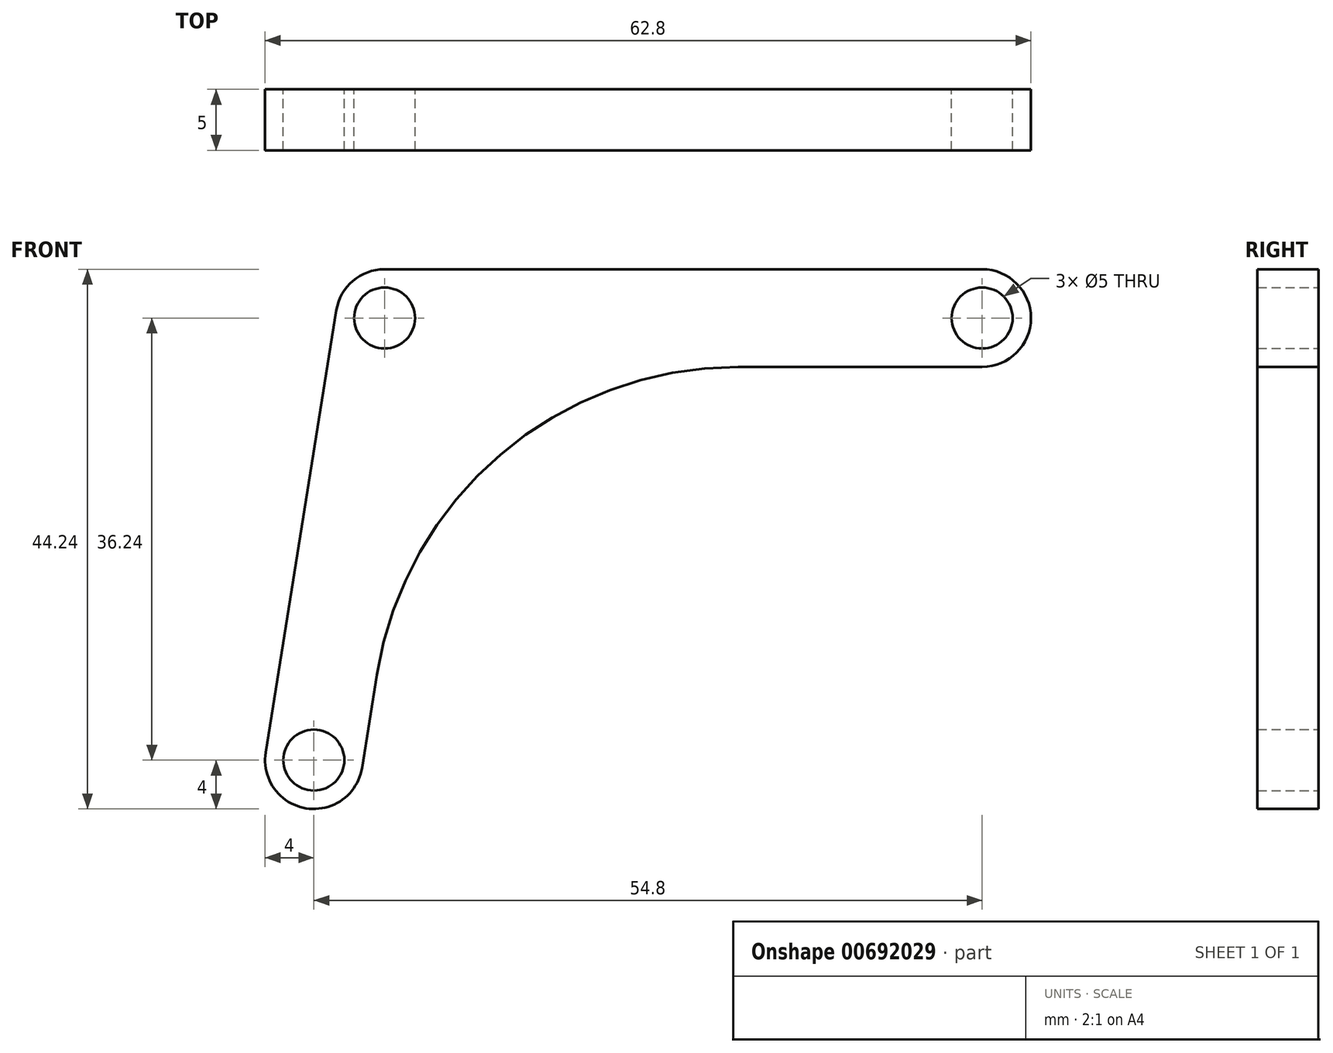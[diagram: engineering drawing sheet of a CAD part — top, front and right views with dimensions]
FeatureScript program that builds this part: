
annotation { "Feature Type Name" : "Feature", "Feature Type Description" : "" }
export const myFeature = defineFeature(function(context is Context, id is Id, definition is map)
    precondition{}
    {
        {
            var Q0;
            Q0=qCreatedBy(makeId("Front.planeOp"),FACE);
            var sketch = newSketch(context, id + "F0", { "sketchPlane" : qUnion([Q0])});
            skArc(sketch, "E0", {"start": v(0, 4) * mm, "mid": v(-2.6, 3.04) * mm, "end": v(-3.95, 0.63) * mm});
            skArc(sketch, "E1", {"start": v(49, -4) * mm, "mid": v(53, 0) * mm, "end": v(49, 4) * mm});
            skArc(sketch, "E2", {"start": v(-9.75, -35.6) * mm, "mid": v(-6.43, -40.19) * mm, "end": v(-1.85, -36.87) * mm});
            skLineSegment(sketch, "E3", {"start": v(0, 4) * mm, "end": v(49, 4) * mm});
            skLineSegment(sketch, "E4", {"start": v(-3.95, 0.63) * mm, "end": v(-9.75, -35.6) * mm});
            skLineSegment(sketch, "E5", {"start": v(-1.85, -36.87) * mm, "end": v(-0.63, -29.26) * mm});
            skLineSegment(sketch, "E6", {"start": v(29, -4) * mm, "end": v(49, -4) * mm});
            skPoint(sketch, "E7.orphan", {"position": v(0, -4) * mm});
            skCircle(sketch, "E8", {"center": v(0, 0) * mm, "radius": 2.5 * mm});
            skCircle(sketch, "E9", {"center": v(-5.8, -36.24) * mm, "radius": 2.5 * mm});
            skCircle(sketch, "E10", {"center": v(49, 0) * mm, "radius": 2.5 * mm});
            skPoint(sketch, "E11.visualSharp", {"position": v(3.41, -4) * mm});
            skArc(sketch, "E11.filletArc", {"start": v(29, -4) * mm, "mid": v(9.53, -11.17) * mm, "end": v(-0.63, -29.26) * mm});
            skSolve(sketch);
        }
        {
            var Q0;
            Q0=makeQuery(id+"F0.imprint","IMPRINT",FACE,{"disambiguationData":[TD([[makeQuery(id+"F0.imprint","IMPRINT",EDGE,{"derivedFrom":sQuery(id+"F0.wireOp",EDGE,"E0")}),1.0]])]});
            extrude(context, id + "F1", {"entities" : qUnion([Q0]), "depth" : 5 * mm, "offsetDistance" : 25 * mm});
        }
    });
